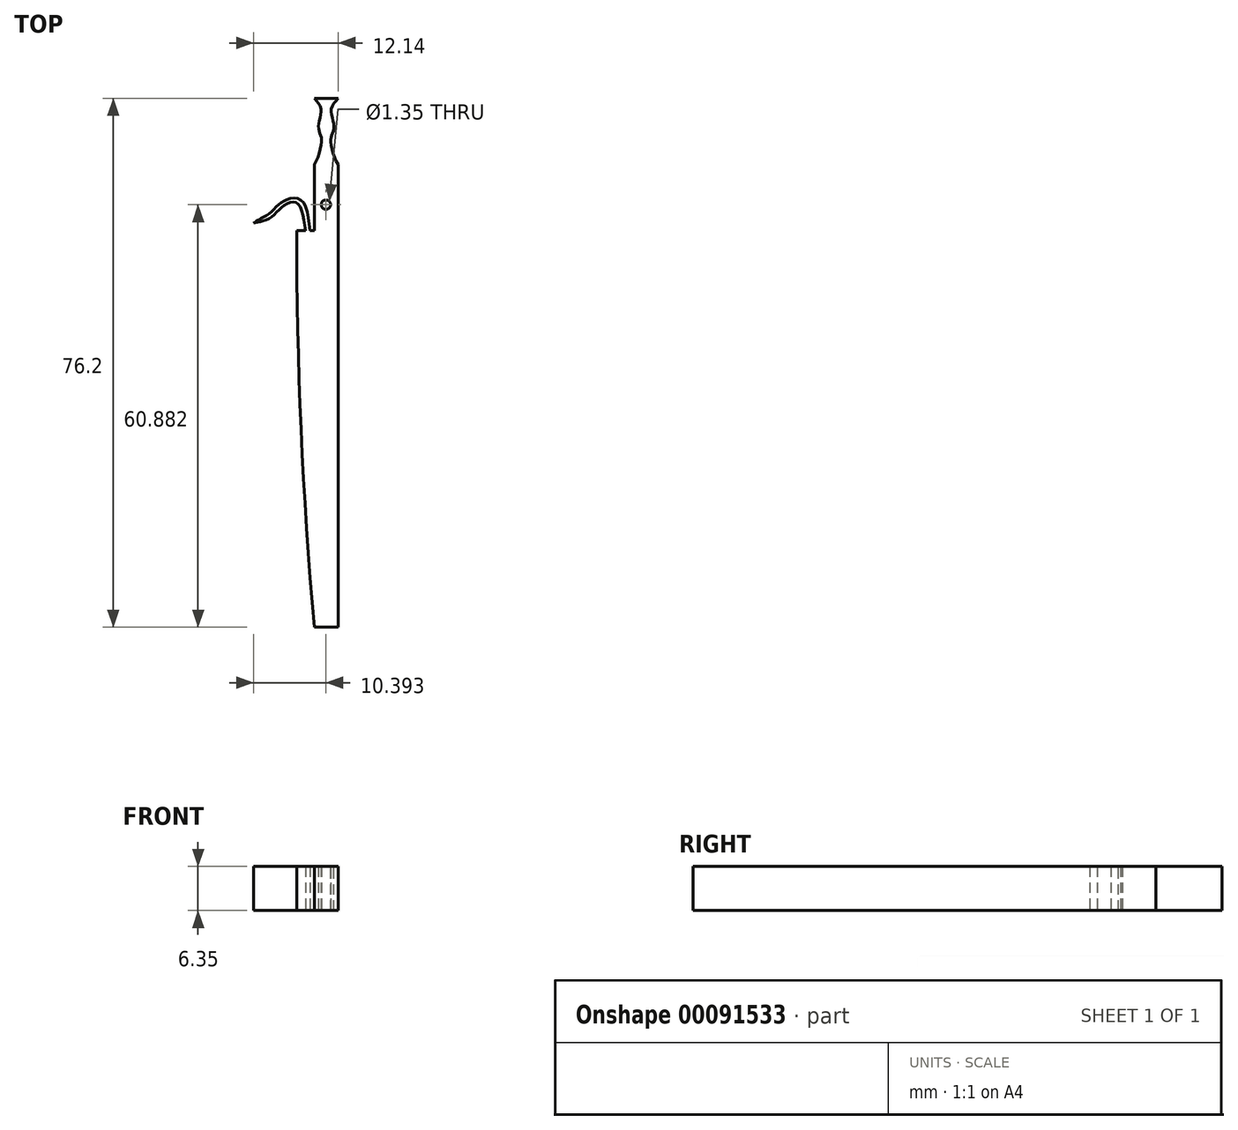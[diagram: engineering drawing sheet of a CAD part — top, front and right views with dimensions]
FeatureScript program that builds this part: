
annotation { "Feature Type Name" : "Feature", "Feature Type Description" : "" }
export const myFeature = defineFeature(function(context is Context, id is Id, definition is map)
    precondition{}
    {
        {
            var Q0;
            Q0=qCreatedBy(makeId("Top.planeOp"),FACE);
            var sketch = newSketch(context, id + "F0", { "sketchPlane" : qUnion([Q0])});
            skLineSegment(sketch, "E0.bottom", {"start": v(0, 0) * mm, "end": v(3.42, 0) * mm});
            skLineSegment(sketch, "E0.top", {"start": v(0, 76.2) * mm, "end": v(3.42, 76.2) * mm});
            skLineSegment(sketch, "E0.left", {"start": v(0, 0) * mm, "end": v(0, 76.2) * mm});
            skLineSegment(sketch, "E0.right", {"start": v(3.42, 0) * mm, "end": v(3.42, 76.2) * mm});
            skLineSegment(sketch, "E1", {"start": v(0, 76.2) * mm, "end": v(0, 57.15) * mm});
            skLineSegment(sketch, "E2.bottom", {"start": v(0, 0) * mm, "end": v(-2.54, 0) * mm, "construction": true});
            skLineSegment(sketch, "E2.top", {"start": v(0, 57.15) * mm, "end": v(-2.54, 57.15) * mm});
            skLineSegment(sketch, "E2.left", {"start": v(0, 0) * mm, "end": v(0, 57.15) * mm});
            skLineSegment(sketch, "E2.right", {"start": v(-2.54, 0) * mm, "end": v(-2.54, 57.15) * mm, "construction": true});
            skArc(sketch, "E3", {"start": v(-2.54, 57.15) * mm, "mid": v(-1.9, 28.55) * mm, "end": v(0, 0) * mm});
            skLineSegment(sketch, "E4", {"start": v(0, 57.15) * mm, "end": v(-1.27, 57.15) * mm});
            skFitSpline(sketch, "E5", {"points": [v(-1.27, 57.15) * mm, v(-2.54, 61.14) * mm, v(-4.48, 60.68) * mm, v(-6.32, 59.01) * mm, v(-8.27, 58.32) * mm, v(-8.9, 58.2) * mm], "startDerivative": vector(-2.63, 18.84) * mm, "endDerivative": vector(-4.82, -0.8) * mm});
            skFitSpline(sketch, "E6", {"points": [v(-0.63, 57.15) * mm, v(-1.83, 61.47) * mm, v(-3.74, 61.7) * mm, v(-5.16, 60.88) * mm, v(-6.34, 59.7) * mm, v(-7.66, 58.92) * mm, v(-8.73, 58.24) * mm], "startDerivative": vector(-2.39, 21.75) * mm, "endDerivative": vector(-7.61, -5.26) * mm});
            skFitSpline(sketch, "E7", {"points": [v(0, 76.2) * mm, v(0.96, 74.66) * mm, v(0.7, 72.97) * mm, v(0.65, 71.64) * mm, v(0.96, 70.72) * mm, v(1.01, 69.65) * mm, v(0, 66.68) * mm], "startDerivative": vector(7.04, -7.96) * mm, "endDerivative": vector(-6.57, -9.7) * mm});
            skLineSegment(sketch, "E8", {"start": v(1.7, 76.2) * mm, "end": v(1.7, 65.75) * mm});
            skFitSpline(sketch, "E9.MirrorCS", {"points": [v(3.42, 76.2) * mm, v(2.46, 74.66) * mm, v(2.71, 72.97) * mm, v(2.76, 71.64) * mm, v(2.46, 70.72) * mm, v(2.4, 69.65) * mm, v(3.42, 66.68) * mm], "startDerivative": vector(-7.04, -7.96) * mm, "endDerivative": vector(6.57, -9.7) * mm});
            skCircle(sketch, "E10", {"center": v(1.67, 60.88) * mm, "radius": 0.68 * mm});
            skSolve(sketch);
        }
        {
            var Q0;
            {var subQ1=sQuery(id+"F0.wireOp",EDGE,"E0.bottom");Q0=makeQuery(id+"F0.imprint","IMPRINT",FACE,{"disambiguationData":[TD([[makeQuery(id+"F0.imprint","IMPRINT",EDGE,{"derivedFrom":subQ1}),1.0]])]});}
            var Q1;
            {var subQ3=sQuery(id+"F0.wireOp",EDGE,"E2.top");Q1=makeQuery(id+"F0.imprint","IMPRINT",FACE,{"disambiguationData":[TD([[makeQuery(id+"F0.imprint","IMPRINT",EDGE,{"derivedFrom":subQ3}),1.0]])]});}
            var Q2;
            {var subQ1=sQuery(id+"F0.wireOp",EDGE,"E4");var subQ3=sQuery(id+"F0.wireOp",EDGE,"E6");var subQ4=makeQuery(id+"F0.imprint","INTERSECT",VERTEX,{"derivedFrom":[subQ1,subQ3]});Q2=makeQuery(id+"F0.imprint","IMPRINT",FACE,{"disambiguationData":[TD([[makeQuery(id+"F0.imprint","IMPRINT",EDGE,{"disambiguationData":[TD([[subQ4,-1.0]])],"derivedFrom":subQ3}),1.0]])]});}
            extrude(context, id + "F1", {"entities" : qUnion([Q0, Q1, Q2]), "depth" : 6.35 * mm});
        }
    });
